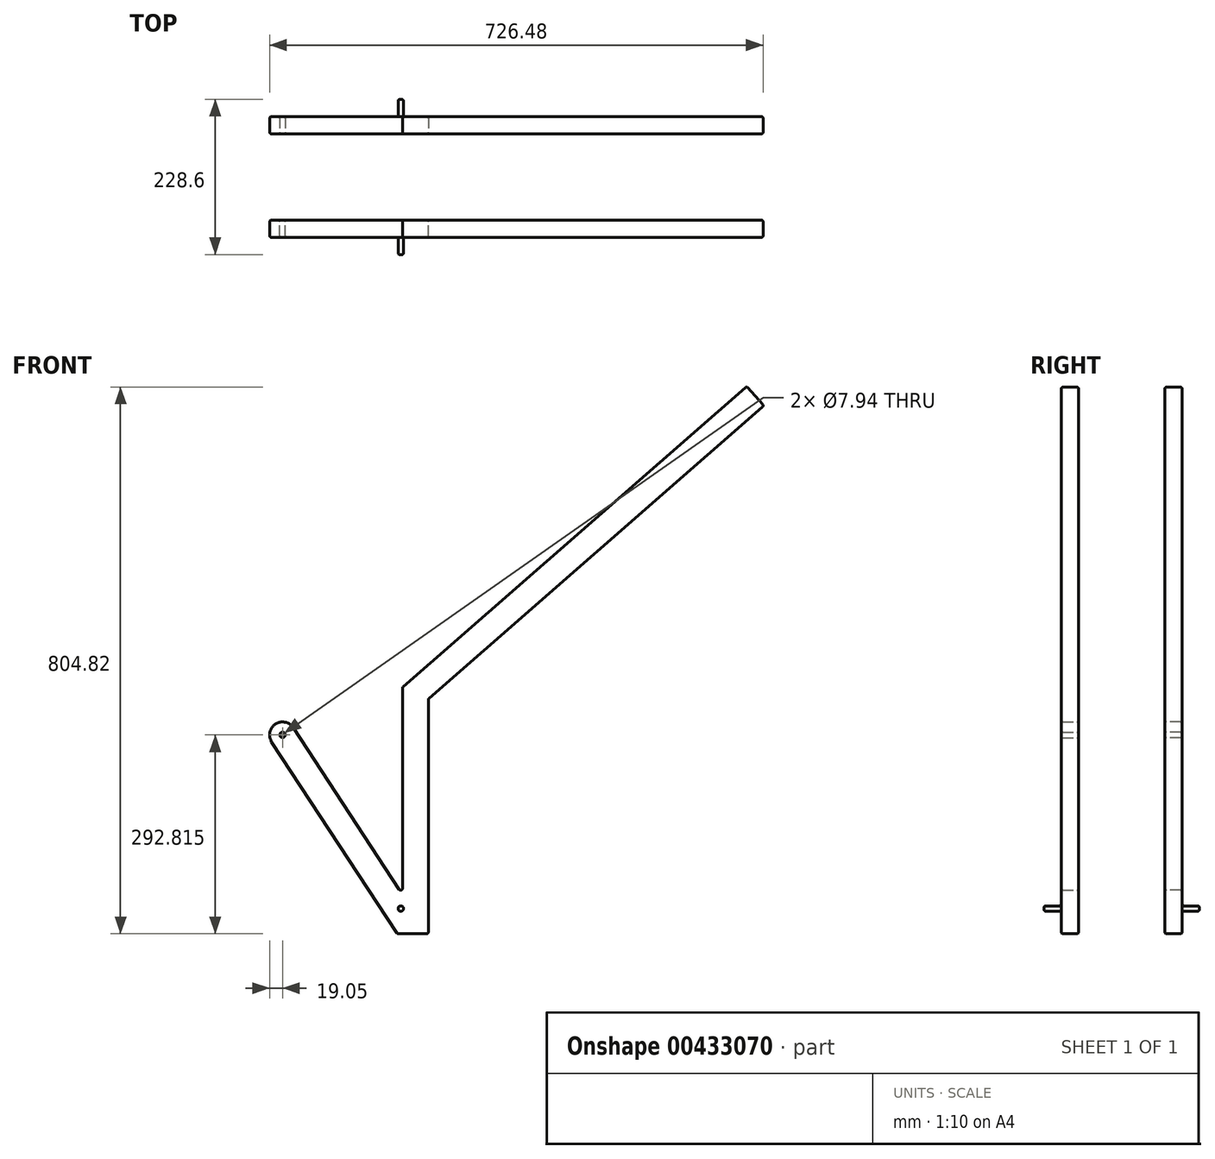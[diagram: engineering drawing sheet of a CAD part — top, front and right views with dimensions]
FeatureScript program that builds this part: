
annotation { "Feature Type Name" : "Feature", "Feature Type Description" : "" }
export const myFeature = defineFeature(function(context is Context, id is Id, definition is map)
    precondition{}
    {
        {
            var Q0;
            Q0=qCreatedBy(makeId("Front.planeOp"),FACE);
            var sketch = newSketch(context, id + "F0", { "sketchPlane" : qUnion([Q0])});
            skCircle(sketch, "E0", {"center": v(-654.05, 384.47) * mm, "radius": 3.97 * mm});
            skCircle(sketch, "E1", {"center": v(-214.67, 292.82) * mm, "radius": 3.97 * mm});
            skLineSegment(sketch, "E2", {"start": v(-230.6, 282.37) * mm, "end": v(-45.55, 0) * mm});
            skArc(sketch, "E3", {"start": v(-198.74, 303.26) * mm, "mid": v(-225.11, 308.75) * mm, "end": v(-230.6, 282.37) * mm});
            skLineSegment(sketch, "E4", {"start": v(-45.55, 0) * mm, "end": v(0, 0) * mm});
            skPoint(sketch, "E5", {"position": v(-38.1, 58.14) * mm});
            skLineSegment(sketch, "E6", {"start": v(-38.1, 362.94) * mm, "end": v(468.74, 805.86) * mm});
            skLineSegment(sketch, "E7", {"start": v(468.74, 805.86) * mm, "end": v(493.8, 777.17) * mm});
            skLineSegment(sketch, "E8", {"start": v(493.8, 777.17) * mm, "end": v(0, 345.63) * mm});
            skLineSegment(sketch, "E9", {"start": v(0, 345.63) * mm, "end": v(0, 0) * mm});
            skLineSegment(sketch, "E10", {"start": v(-198.74, 303.26) * mm, "end": v(-38.1, 58.14) * mm});
            skLineSegment(sketch, "E11", {"start": v(-38.1, 362.94) * mm, "end": v(-38.1, 58.14) * mm});
            skCircle(sketch, "E12", {"center": v(-40.53, 37.23) * mm, "radius": 3.97 * mm});
            skSolve(sketch);
        }
        {
            var Q0;
            Q0=makeQuery(id+"F0.imprint","IMPRINT",FACE,{"disambiguationData":[TD([[makeQuery(id+"F0.imprint","IMPRINT",EDGE,{"derivedFrom":sQuery(id+"F0.wireOp",EDGE,"E12")}),1.0]])]});
            extrude(context, id + "F1", {"entities" : qUnion([Q0]), "depth" : 50.8 * mm});
        }
        {
            var Q0;
            Q0=makeQuery(id+"F0.imprint","IMPRINT",FACE,{"disambiguationData":[TD([[makeQuery(id+"F0.imprint","IMPRINT",EDGE,{"derivedFrom":sQuery(id+"F0.wireOp",EDGE,"E1")}),-1.0]])]});
            extrude(context, id + "F2", {"entities" : qUnion([Q0]), "operationType" : NewBodyOperationType.ADD, "depth" : 25.4 * mm});
        }
        {
            var Q0;
            Q0=makeQuery(id+"F2.opExtrude","SWEPT_FACE",FACE,{"disambiguationData":[OSD([sQuery(id+"F0.wireOp",EDGE,"E11")])]});
            var Q1;
            Q1=makeQuery(id+"F2.opExtrude","SWEPT_FACE",FACE,{"disambiguationData":[OSD([sQuery(id+"F0.wireOp",EDGE,"E9")])]});
            var Q2;
            Q2=makeQuery(id+"F2.opExtrude","SWEPT_FACE",FACE,{"disambiguationData":[OSD([sQuery(id+"F0.wireOp",EDGE,"E10")])]});
            var Q3;
            Q3=makeQuery(id+"F2.opExtrude","CAP_EDGE",EDGE,{"disambiguationData":[OSD([sQuery(id+"F0.wireOp",EDGE,"E9")])],"isStart":false});
            var Q4;
            Q4=makeQuery(id+"F2.opExtrude","SWEPT_FACE",FACE,{"disambiguationData":[OSD([sQuery(id+"F0.wireOp",EDGE,"E2")])]});
            var Q5;
            Q5=makeQuery(id+"F2.opExtrude","CAP_FACE",FACE,{"disambiguationData":[OSD([sQuery(id+"F0.wireOp",EDGE,"E1"),sQuery(id+"F0.wireOp",EDGE,"E2"),sQuery(id+"F0.wireOp",EDGE,"E3"),sQuery(id+"F0.wireOp",EDGE,"E4"),sQuery(id+"F0.wireOp",EDGE,"E6"),sQuery(id+"F0.wireOp",EDGE,"E7"),sQuery(id+"F0.wireOp",EDGE,"E8"),sQuery(id+"F0.wireOp",EDGE,"E9"),sQuery(id+"F0.wireOp",EDGE,"E10"),sQuery(id+"F0.wireOp",EDGE,"E11"),sQuery(id+"F0.wireOp",EDGE,"E12")])],"isStart":false});
            var Q6;
            Q6=makeQuery(id+"F2.opExtrude","CAP_EDGE",EDGE,{"disambiguationData":[OSD([sQuery(id+"F0.wireOp",EDGE,"E8")])],"isStart":false});
            var Q7;
            Q7=makeQuery(id+"F2.opExtrude","CAP_EDGE",EDGE,{"disambiguationData":[OSD([sQuery(id+"F0.wireOp",EDGE,"E2")])],"isStart":false});
            var Q8;
            Q8=makeQuery(id+"F2.opExtrude","CAP_EDGE",EDGE,{"disambiguationData":[OSD([sQuery(id+"F0.wireOp",EDGE,"E11")])],"isStart":true});
            var Q9;
            Q9=makeQuery(id+"F2.opExtrude","CAP_EDGE",EDGE,{"disambiguationData":[OSD([sQuery(id+"F0.wireOp",EDGE,"E6")])],"isStart":true});
            var Q10;
            Q10=makeQuery(id+"F2.opExtrude","CAP_EDGE",EDGE,{"disambiguationData":[OSD([sQuery(id+"F0.wireOp",EDGE,"E6")])],"isStart":false});
            var Q11;
            Q11=makeQuery(id+"F2.opExtrude","CAP_EDGE",EDGE,{"disambiguationData":[OSD([sQuery(id+"F0.wireOp",EDGE,"E2")])],"isStart":true});
            var Q12;
            {var subQ0=sQuery(id+"F0.wireOp",EDGE,"E12");Q12=makeQuery(id+"F2.boolean.opBoolean","MERGE",FACE,{"derivedFrom":[makeQuery(id+"F1.opExtrude","CAP_FACE",FACE,{"disambiguationData":[OSD([subQ0])],"isStart":true}),makeQuery(id+"F2.opExtrude","CAP_FACE",FACE,{"disambiguationData":[OSD([sQuery(id+"F0.wireOp",EDGE,"E1"),sQuery(id+"F0.wireOp",EDGE,"E2"),sQuery(id+"F0.wireOp",EDGE,"E3"),sQuery(id+"F0.wireOp",EDGE,"E4"),sQuery(id+"F0.wireOp",EDGE,"E6"),sQuery(id+"F0.wireOp",EDGE,"E7"),sQuery(id+"F0.wireOp",EDGE,"E8"),sQuery(id+"F0.wireOp",EDGE,"E9"),sQuery(id+"F0.wireOp",EDGE,"E10"),sQuery(id+"F0.wireOp",EDGE,"E11"),subQ0])],"isStart":true})]});}
            var Q13;
            Q13=makeQuery(id+"F2.opExtrude","CAP_EDGE",EDGE,{"disambiguationData":[OSD([sQuery(id+"F0.wireOp",EDGE,"E11")])],"isStart":false});
            var Q14;
            Q14=makeQuery(id+"F2.opExtrude","SWEPT_FACE",FACE,{"disambiguationData":[OSD([sQuery(id+"F0.wireOp",EDGE,"E8")])]});
            var Q15;
            Q15=makeQuery(id+"F2.opExtrude","CAP_EDGE",EDGE,{"disambiguationData":[OSD([sQuery(id+"F0.wireOp",EDGE,"E10")])],"isStart":false});
            var Q16;
            Q16=makeQuery(id+"F2.opExtrude","SWEPT_FACE",FACE,{"disambiguationData":[OSD([sQuery(id+"F0.wireOp",EDGE,"E6")])]});
            var Q17;
            Q17=makeQuery(id+"F2.opExtrude","CAP_EDGE",EDGE,{"disambiguationData":[OSD([sQuery(id+"F0.wireOp",EDGE,"E8")])],"isStart":true});
            var Q18;
            Q18=makeQuery(id+"F2.opExtrude","CAP_EDGE",EDGE,{"disambiguationData":[OSD([sQuery(id+"F0.wireOp",EDGE,"E9")])],"isStart":true});
            var Q19;
            Q19=makeQuery(id+"F2.opExtrude","CAP_EDGE",EDGE,{"disambiguationData":[OSD([sQuery(id+"F0.wireOp",EDGE,"E10")])],"isStart":true});
            var Q20;
            Q20=makeQuery(id+"F2.opExtrude","SWEPT_FACE",FACE,{"disambiguationData":[OSD([sQuery(id+"F0.wireOp",EDGE,"E7")])]});
            var Q21;
            Q21=makeQuery(id+"F2.opExtrude","CAP_EDGE",EDGE,{"disambiguationData":[OSD([sQuery(id+"F0.wireOp",EDGE,"E7")])],"isStart":false});
            var Q22;
            Q22=makeQuery(id+"F2.opExtrude","SWEPT_EDGE",EDGE,{"disambiguationData":[OSD([sQuery(id+"F0.wireOp",EDGE,"E8"),sQuery(id+"F0.wireOp",EDGE,"E9")])]});
            var Q23;
            Q23=makeQuery(id+"F2.opExtrude","SWEPT_EDGE",EDGE,{"disambiguationData":[OSD([sQuery(id+"F0.wireOp",EDGE,"E7"),sQuery(id+"F0.wireOp",EDGE,"E8")])]});
            var Q24;
            Q24=makeQuery(id+"F2.opExtrude","SWEPT_FACE",FACE,{"disambiguationData":[OSD([sQuery(id+"F0.wireOp",EDGE,"E4")])]});
            var Q25;
            Q25=makeQuery(id+"F2.opExtrude","SWEPT_EDGE",EDGE,{"disambiguationData":[OSD([sQuery(id+"F0.wireOp",EDGE,"E6"),sQuery(id+"F0.wireOp",EDGE,"E7")])]});
            var Q26;
            Q26=makeQuery(id+"F2.opExtrude","SWEPT_EDGE",EDGE,{"disambiguationData":[OSD([sQuery(id+"F0.wireOp",EDGE,"E6"),sQuery(id+"F0.wireOp",EDGE,"E11")])]});
            var Q27;
            Q27=makeQuery(id+"F1.opExtrude","SWEPT_FACE",FACE,{"disambiguationData":[OSD([sQuery(id+"F0.wireOp",EDGE,"E12")])]});
            var Q28;
            Q28=makeQuery(id+"F2.opExtrude","CAP_EDGE",EDGE,{"disambiguationData":[OSD([sQuery(id+"F0.wireOp",EDGE,"E4")])],"isStart":false});
            var Q29;
            Q29=makeQuery(id+"F2.opExtrude","CAP_EDGE",EDGE,{"disambiguationData":[OSD([sQuery(id+"F0.wireOp",EDGE,"E7")])],"isStart":true});
            var Q30;
            Q30=makeQuery(id+"F2.opExtrude","SWEPT_EDGE",EDGE,{"disambiguationData":[OSD([sQuery(id+"F0.wireOp",EDGE,"E2"),sQuery(id+"F0.wireOp",EDGE,"E4")])]});
            var Q31;
            Q31=makeQuery(id+"F1.opExtrude","CAP_FACE",FACE,{"disambiguationData":[OSD([sQuery(id+"F0.wireOp",EDGE,"E12")])],"isStart":false});
            var Q32;
            Q32=makeQuery(id+"F2.opExtrude","SWEPT_EDGE",EDGE,{"disambiguationData":[OSD([sQuery(id+"F0.wireOp",EDGE,"E4"),sQuery(id+"F0.wireOp",EDGE,"E9")])]});
            var Q33;
            Q33=makeQuery(id+"F2.opExtrude","SWEPT_FACE",FACE,{"disambiguationData":[OSD([sQuery(id+"F0.wireOp",EDGE,"E3")])]});
            var Q34;
            Q34=makeQuery(id+"F2.opExtrude","CAP_EDGE",EDGE,{"disambiguationData":[OSD([sQuery(id+"F0.wireOp",EDGE,"E4")])],"isStart":true});
            var Q35;
            Q35=makeQuery(id+"F1.opExtrude","CAP_EDGE",EDGE,{"disambiguationData":[OSD([sQuery(id+"F0.wireOp",EDGE,"E12")])],"isStart":false});
            var Q36;
            Q36=makeQuery(id+"F2.opExtrude","CAP_EDGE",EDGE,{"disambiguationData":[OSD([sQuery(id+"F0.wireOp",EDGE,"E12")])],"isStart":false});
            var Q37;
            Q37=makeQuery(id+"F2.opExtrude","SWEPT_FACE",FACE,{"disambiguationData":[OSD([sQuery(id+"F0.wireOp",EDGE,"E1")])]});
            var Q38;
            Q38=makeQuery(id+"F2.opExtrude","CAP_EDGE",EDGE,{"disambiguationData":[OSD([sQuery(id+"F0.wireOp",EDGE,"E3")])],"isStart":false});
            var Q39;
            Q39=makeQuery(id+"F2.opExtrude","SWEPT_EDGE",EDGE,{"disambiguationData":[OSD([sQuery(id+"F0.wireOp",EDGE,"E10"),sQuery(id+"F0.wireOp",EDGE,"E11")])]});
            var Q40;
            Q40=makeQuery(id+"F2.opExtrude","CAP_EDGE",EDGE,{"disambiguationData":[OSD([sQuery(id+"F0.wireOp",EDGE,"E1")])],"isStart":false});
            var Q41;
            Q41=makeQuery(id+"F2.opExtrude","SWEPT_EDGE",EDGE,{"disambiguationData":[OSD([sQuery(id+"F0.wireOp",EDGE,"E2"),sQuery(id+"F0.wireOp",EDGE,"E3")])]});
            var Q42;
            Q42=makeQuery(id+"F2.opExtrude","SWEPT_EDGE",EDGE,{"disambiguationData":[OSD([sQuery(id+"F0.wireOp",EDGE,"E3"),sQuery(id+"F0.wireOp",EDGE,"E10")])]});
            var Q43;
            Q43=makeQuery(id+"F2.opExtrude","CAP_EDGE",EDGE,{"disambiguationData":[OSD([sQuery(id+"F0.wireOp",EDGE,"E3")])],"isStart":true});
            var Q44;
            Q44=makeQuery(id+"F2.opExtrude","CAP_EDGE",EDGE,{"disambiguationData":[OSD([sQuery(id+"F0.wireOp",EDGE,"E1")])],"isStart":true});
            fillet(context, id + "F3", {"entities" : qUnion([Q0, Q1, Q2, Q3, Q4, Q5, Q6, Q7, Q8, Q9, Q10, Q11, Q12, Q13, Q14, Q15, Q16, Q17, Q18, Q19, Q20, Q21, Q22, Q23, Q24, Q25, Q26, Q27, Q28, Q29, Q30, Q31, Q32, Q33, Q34, Q35, Q36, Q37, Q38, Q39, Q40, Q41, Q42, Q43, Q44]), "radius" : 2.54 * mm, "tangentPropagation" : true, "allowEdgeOverflow" : false});
        }
        {
            var Q0;
            Q0=makeQuery(id+"F1.opExtrude","SWEPT_BODY",BODY,{"disambiguationData":[OSD([sQuery(id+"F0.wireOp",EDGE,"E12")])]});
            transform(context, id + "F4", {"entities" : qUnion([Q0]), "transformType" : TransformType.TRANSLATION_3D, "dx" : 0 * mm, "dy" : 127 * mm, "dz" : 0 * mm, "makeCopy" : true});
        }
        {
            var Q0;
            Q0=makeQuery(id+"F4.opPattern","COPY",BODY,{"derivedFrom":makeQuery(id+"F1.opExtrude","SWEPT_BODY",BODY,{"disambiguationData":[OSD([sQuery(id+"F0.wireOp",EDGE,"E12")])]}),"instanceName":"1"});
            var Q1;
            {var subQ0=sQuery(id+"F0.wireOp",EDGE,"E12");Q1=makeQuery(id+"F4.opPattern","COPY",FACE,{"derivedFrom":makeQuery(id+"F2.boolean.opBoolean","MERGE",FACE,{"derivedFrom":[makeQuery(id+"F1.opExtrude","CAP_FACE",FACE,{"disambiguationData":[OSD([subQ0])],"isStart":true}),makeQuery(id+"F2.opExtrude","CAP_FACE",FACE,{"disambiguationData":[OSD([sQuery(id+"F0.wireOp",EDGE,"E1"),sQuery(id+"F0.wireOp",EDGE,"E2"),sQuery(id+"F0.wireOp",EDGE,"E3"),sQuery(id+"F0.wireOp",EDGE,"E4"),sQuery(id+"F0.wireOp",EDGE,"E6"),sQuery(id+"F0.wireOp",EDGE,"E7"),sQuery(id+"F0.wireOp",EDGE,"E8"),sQuery(id+"F0.wireOp",EDGE,"E9"),sQuery(id+"F0.wireOp",EDGE,"E10"),sQuery(id+"F0.wireOp",EDGE,"E11"),subQ0])],"isStart":true})]}),"instanceName":"1"});}
            mirror(context, id + "F5", {"entities" : qUnion([Q0]), "mirrorPlane" : qUnion([Q1])});
        }
        {
            var Q0;
            Q0=makeQuery(id+"F4.opPattern","COPY",BODY,{"derivedFrom":makeQuery(id+"F1.opExtrude","SWEPT_BODY",BODY,{"disambiguationData":[OSD([sQuery(id+"F0.wireOp",EDGE,"E12")])]}),"instanceName":"1"});
            deleteBodies(context, id + "F6", {"entities" : qUnion([Q0])});
        }
    });
